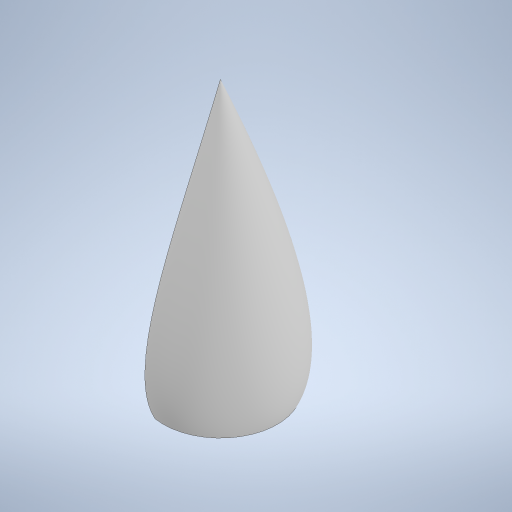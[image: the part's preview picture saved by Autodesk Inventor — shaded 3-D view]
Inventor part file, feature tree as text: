
AUTODESK INVENTOR PART (.ipt)
format: ipt  version: 2023 (Build 270158000, 158)  size: 333,824 bytes
history: native  units: mm
features: sketch x5, extrude x3, other x1, revolve x1, hole x1, fillet x1
ambient origin geometry x8: Origin, YZ Plane, XZ Plane, XY Plane, X Axis, Y Axis, Z Axis, Center Point
bodies: Body1 (feature_tree)
feature tree (12):
  other  "ソリッド1"
  revolve  "回転1"
  extrude  "押し出し3"  Depth=40.0mm
  hole  "穴1"  [1 undecoded]
  extrude  "押し出し4"  Depth=45.0mm
  extrude  "押し出し5"  Depth=40.0mm
  fillet  "フィレット2"  [1 undecoded]
  sketch  "スケッチ1"
  sketch  "スケッチ4"
  sketch  "スケッチ5"
  sketch  "スケッチ6"
  sketch  "スケッチ7"
note: 2 required parameter values undecoded (feature->parameter linkage not recoverable at this tier; creation-order binding heuristic only, values carry confidence <= 0.55)
